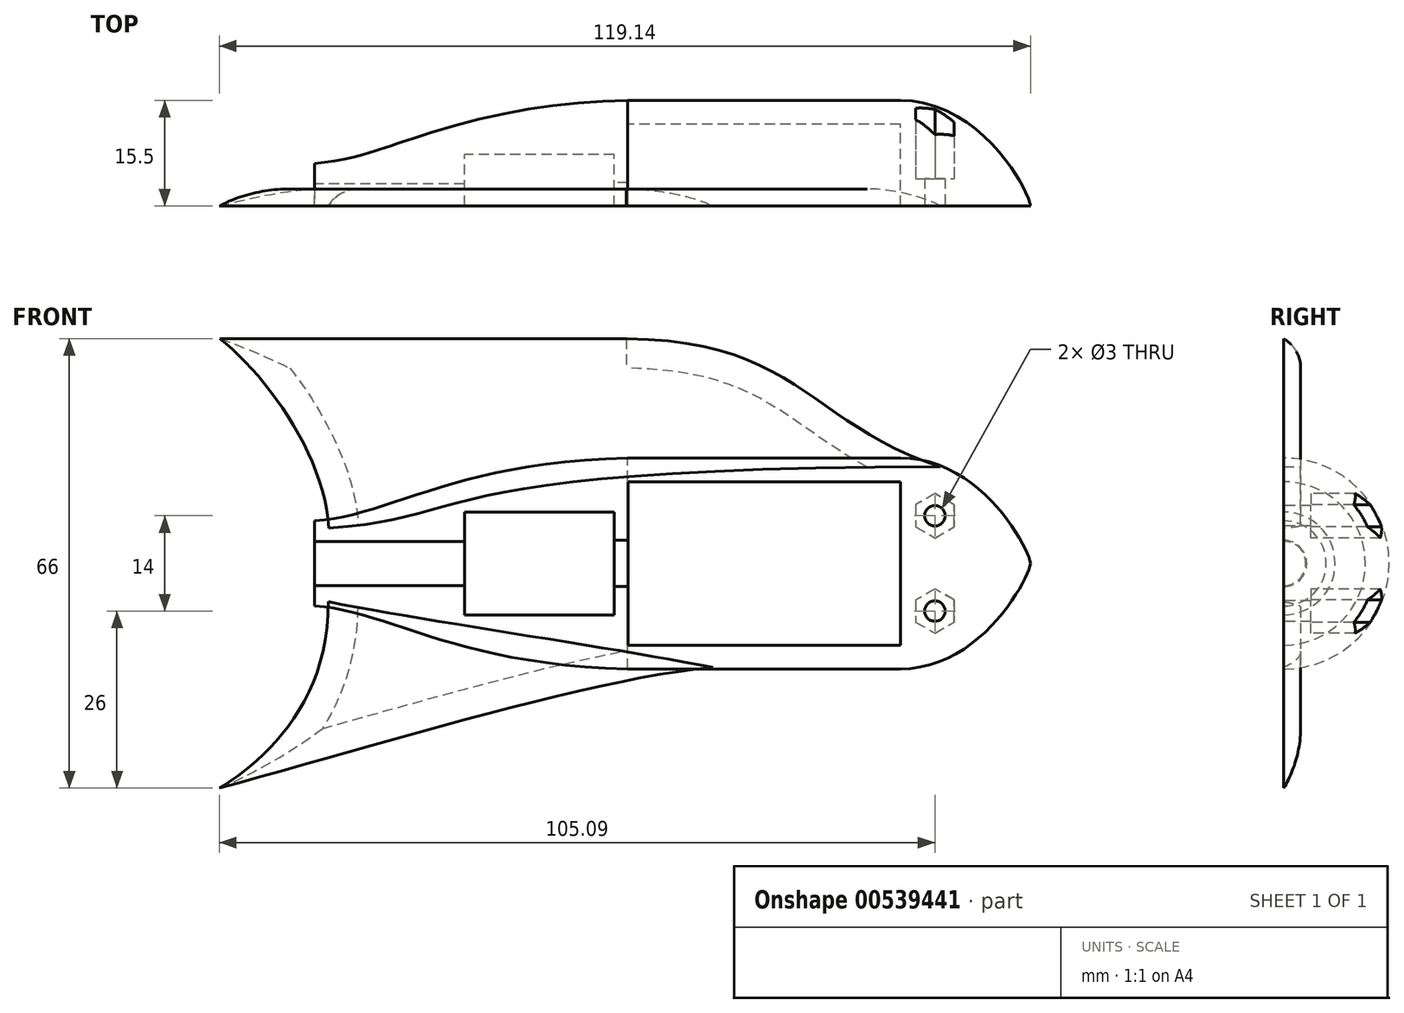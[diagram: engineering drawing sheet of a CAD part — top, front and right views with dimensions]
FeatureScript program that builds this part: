
annotation { "Feature Type Name" : "Feature", "Feature Type Description" : "" }
export const myFeature = defineFeature(function(context is Context, id is Id, definition is map)
    precondition{}
    {
        {
            var Q0;
            Q0=qCreatedBy(makeId("Front.planeOp"),FACE);
            var sketch = newSketch(context, id + "F0", { "sketchPlane" : qUnion([Q0])});
            skLineSegment(sketch, "E0", {"start": v(-75.09, 3.25) * mm, "end": v(-53.09, 3.25) * mm});
            skLineSegment(sketch, "E1", {"start": v(-53.09, 3.25) * mm, "end": v(-53.09, 7.55) * mm});
            skLineSegment(sketch, "E2", {"start": v(-53.09, 7.55) * mm, "end": v(-31.09, 7.55) * mm});
            skLineSegment(sketch, "E3", {"start": v(-31.09, 7.55) * mm, "end": v(-31.09, 3.4) * mm});
            skLineSegment(sketch, "E4", {"start": v(-31.09, 3.4) * mm, "end": v(-29.09, 3.4) * mm});
            skLineSegment(sketch, "E5", {"start": v(-29.09, 3.4) * mm, "end": v(-29.09, 12) * mm});
            skLineSegment(sketch, "E6", {"start": v(-29.09, 12) * mm, "end": v(10.91, 12) * mm});
            skLineSegment(sketch, "E7", {"start": v(10.91, 12) * mm, "end": v(10.91, 0) * mm});
            skLineSegment(sketch, "E8", {"start": v(10.91, 0) * mm, "end": v(30.05, 0) * mm});
            skLineSegment(sketch, "E9", {"start": v(-75.09, 6.25) * mm, "end": v(-75.09, 3.25) * mm});
            skLineSegment(sketch, "E10", {"start": v(10.91, 15.5) * mm, "end": v(-29.14, 15.5) * mm});
            skFitSpline(sketch, "E11", {"points": [v(30.05, 0) * mm, v(10.91, 15.5) * mm], "startDerivative": vector(-1.53, 7.93) * mm, "endDerivative": vector(-35.34, 0.06) * mm});
            skLineSegment(sketch, "E12", {"start": v(-31.09, 3.4) * mm, "end": v(-31.09, 0) * mm});
            skFitSpline(sketch, "E13", {"points": [v(-29.14, 15.5) * mm, v(-75.09, 6.25) * mm], "startDerivative": vector(-76.48, -1.84) * mm, "endDerivative": vector(-32.8, -2) * mm});
            skLineSegment(sketch, "E14", {"start": v(-53.09, 3.25) * mm, "end": v(-53.09, 0) * mm});
            skSolve(sketch);
        }
        {
            var Q0;
            Q0=makeQuery(id+"F0.imprint","IMPRINT",FACE,{"disambiguationData":[TD([[makeQuery(id+"F0.imprint","IMPRINT",EDGE,{"derivedFrom":sQuery(id+"F0.wireOp",EDGE,"E0")}),1.0]])]});
            var Q1;
            Q1=sQuery(id+"F0.wireOp",EDGE,"E8");
            revolve(context, id + "F1", {"entities" : qUnion([Q0]), "axis" : qUnion([Q1]), "revolveType" : RevolveType.ONE_DIRECTION, "angle" : 180 * degree});
        }
        {
            var Q0;
            Q0=qCreatedBy(makeId("Front.planeOp"),FACE);
            var sketch = newSketch(context, id + "F2", { "sketchPlane" : qUnion([Q0])});
            skFitSpline(sketch, "E15.MirrorCS", {"points": [v(-89.1, -33) * mm, v(-73.1, -5.62) * mm], "startDerivative": vector(19.99, 12.25) * mm, "endDerivative": vector(-0.31, 44.72) * mm});
            skFitSpline(sketch, "E16.MirrorCS", {"points": [v(-73.1, -5.63) * mm, v(-16.62, -15.27) * mm], "startDerivative": vector(45.64, -9.01) * mm, "endDerivative": vector(45.64, -9.01) * mm});
            skFitSpline(sketch, "E17", {"points": [v(-16.62, -15.27) * mm, v(-89.1, -33) * mm], "startDerivative": vector(-54.11, -4.81) * mm, "endDerivative": vector(-66.28, -18) * mm});
            skSolve(sketch);
        }
        {
            var Q0;
            Q0=qCreatedBy(makeId("Front.planeOp"),FACE);
            var sketch = newSketch(context, id + "F3", { "sketchPlane" : qUnion([Q0])});
            skFitSpline(sketch, "E18", {"points": [v(-72.99, 5.2) * mm, v(16.8, 14.22) * mm], "startDerivative": vector(68.22, 4.63) * mm, "endDerivative": vector(232.35, 0.67) * mm});
            skFitSpline(sketch, "E19", {"points": [v(16.8, 14.22) * mm, v(-29.28, 33) * mm], "startDerivative": vector(-57.2, 18.37) * mm, "endDerivative": vector(-76.22, 0.95) * mm});
            skFitSpline(sketch, "E20", {"points": [v(-29.28, 33) * mm, v(-88.99, 33) * mm], "startDerivative": vector(-55.16, 0) * mm, "endDerivative": vector(-55.16, 0) * mm});
            skFitSpline(sketch, "E21", {"points": [v(-88.99, 33) * mm, v(-72.99, 5.2) * mm], "startDerivative": vector(21.07, -16.51) * mm, "endDerivative": vector(1.77, -31.08) * mm});
            skSolve(sketch);
        }
        {
            var Q0;
            Q0=qSketchRegion(id+"F3",true);
            extrude(context, id + "F4", {"entities" : qUnion([Q0]), "depth" : 2.5 * mm, "offsetDistance" : 25 * mm});
        }
        {
            var Q0;
            Q0=makeQuery(id+"F4.opExtrude","CAP_EDGE",EDGE,{"disambiguationData":[OSD([sQuery(id+"F3.wireOp",EDGE,"E20")])],"isStart":false});
            var Q1;
            Q1=makeQuery(id+"F4.opExtrude","CAP_EDGE",EDGE,{"disambiguationData":[OSD([sQuery(id+"F3.wireOp",EDGE,"E19")])],"isStart":false});
            fillet(context, id + "F5", {"entities" : qUnion([Q0, Q1]), "radius" : 5 * mm, "tangentPropagation" : true, "allowEdgeOverflow" : false});
        }
        {
            var Q0;
            Q0=makeQuery(id+"F5.opFillet","BLEND_EDGE",EDGE,{"blendedFrom":[makeQuery(id+"F4.opExtrude","CAP_EDGE",EDGE,{"disambiguationData":[OSD([sQuery(id+"F3.wireOp",EDGE,"E20")])],"isStart":false}),makeQuery(id+"F4.opExtrude","SWEPT_FACE",FACE,{"disambiguationData":[OSD([sQuery(id+"F3.wireOp",EDGE,"E21")])]})],"blendedInto":[makeQuery(id+"F4.opExtrude","SWEPT_FACE",FACE,{"disambiguationData":[OSD([sQuery(id+"F3.wireOp",EDGE,"E21")])]})]});
            fillet(context, id + "F6", {"entities" : qUnion([Q0]), "radius" : 5 * mm, "tangentPropagation" : true, "allowEdgeOverflow" : false});
        }
        {
            var Q0;
            Q0=makeQuery(id+"F2.imprint","IMPRINT",FACE,{"disambiguationData":[TD([[makeQuery(id+"F2.imprint","IMPRINT",EDGE,{"derivedFrom":sQuery(id+"F2.wireOp",EDGE,"E15.MirrorCS")}),-1.0]])]});
            extrude(context, id + "F7", {"entities" : qUnion([Q0]), "depth" : 2.5 * mm, "offsetDistance" : 25 * mm});
        }
        {
            var Q0;
            Q0=makeQuery(id+"F7.opExtrude","CAP_EDGE",EDGE,{"disambiguationData":[OSD([sQuery(id+"F2.wireOp",EDGE,"E15.MirrorCS")])],"isStart":false});
            fillet(context, id + "F8", {"entities" : qUnion([Q0]), "radius" : 5 * mm, "tangentPropagation" : true, "allowEdgeOverflow" : false});
        }
        {
            var Q0;
            Q0=makeQuery(id+"F7.opExtrude","CAP_EDGE",EDGE,{"disambiguationData":[OSD([sQuery(id+"F2.wireOp",EDGE,"E17")])],"isStart":false});
            fillet(context, id + "F9", {"entities" : qUnion([Q0]), "radius" : 5 * mm, "tangentPropagation" : true, "allowEdgeOverflow" : false});
        }
        {
            var Q0;
            Q0=makeQuery(id+"F1.opRevolve","SWEPT_BODY",BODY,{"disambiguationData":[OSD([sQuery(id+"F0.wireOp",EDGE,"E0"),sQuery(id+"F0.wireOp",EDGE,"E1"),sQuery(id+"F0.wireOp",EDGE,"E2"),sQuery(id+"F0.wireOp",EDGE,"E3"),sQuery(id+"F0.wireOp",EDGE,"E4"),sQuery(id+"F0.wireOp",EDGE,"E5"),sQuery(id+"F0.wireOp",EDGE,"E6"),sQuery(id+"F0.wireOp",EDGE,"E7"),sQuery(id+"F0.wireOp",EDGE,"E8"),sQuery(id+"F0.wireOp",EDGE,"E9"),sQuery(id+"F0.wireOp",EDGE,"E10"),sQuery(id+"F0.wireOp",EDGE,"E11"),sQuery(id+"F0.wireOp",EDGE,"E13")])]});
            var Q1;
            Q1=makeQuery(id+"F7.opExtrude","SWEPT_BODY",BODY,{"disambiguationData":[OSD([sQuery(id+"F2.wireOp",EDGE,"E15.MirrorCS"),sQuery(id+"F2.wireOp",EDGE,"E16.MirrorCS"),sQuery(id+"F2.wireOp",EDGE,"E17")])]});
            var Q2;
            Q2=makeQuery(id+"F4.opExtrude","SWEPT_BODY",BODY,{"disambiguationData":[OSD([sQuery(id+"F3.wireOp",EDGE,"E18"),sQuery(id+"F3.wireOp",EDGE,"E19"),sQuery(id+"F3.wireOp",EDGE,"E20"),sQuery(id+"F3.wireOp",EDGE,"E21")])]});
            var Q3;
            Q3=qCreatedBy(makeId("Front.planeOp"),FACE);
            mirror(context, id + "F10", {"entities" : qUnion([Q0, Q1, Q2]), "mirrorPlane" : qUnion([Q3])});
        }
        {
            var Q0;
            Q0=makeQuery(id+"F1.opRevolve","SWEPT_BODY",BODY,{"disambiguationData":[OSD([sQuery(id+"F0.wireOp",EDGE,"E0"),sQuery(id+"F0.wireOp",EDGE,"E1"),sQuery(id+"F0.wireOp",EDGE,"E2"),sQuery(id+"F0.wireOp",EDGE,"E3"),sQuery(id+"F0.wireOp",EDGE,"E4"),sQuery(id+"F0.wireOp",EDGE,"E5"),sQuery(id+"F0.wireOp",EDGE,"E6"),sQuery(id+"F0.wireOp",EDGE,"E7"),sQuery(id+"F0.wireOp",EDGE,"E8"),sQuery(id+"F0.wireOp",EDGE,"E9"),sQuery(id+"F0.wireOp",EDGE,"E10"),sQuery(id+"F0.wireOp",EDGE,"E11"),sQuery(id+"F0.wireOp",EDGE,"E13")])]});
            var Q1;
            Q1=makeQuery(id+"F4.opExtrude","SWEPT_BODY",BODY,{"disambiguationData":[OSD([sQuery(id+"F3.wireOp",EDGE,"E18"),sQuery(id+"F3.wireOp",EDGE,"E19"),sQuery(id+"F3.wireOp",EDGE,"E20"),sQuery(id+"F3.wireOp",EDGE,"E21")])]});
            var Q2;
            Q2=makeQuery(id+"F7.opExtrude","SWEPT_BODY",BODY,{"disambiguationData":[OSD([sQuery(id+"F2.wireOp",EDGE,"E15.MirrorCS"),sQuery(id+"F2.wireOp",EDGE,"E16.MirrorCS"),sQuery(id+"F2.wireOp",EDGE,"E17")])]});
            deleteBodies(context, id + "F11", {"entities" : qUnion([Q0, Q1, Q2])});
        }
        {
            var Q0;
            Q0=qCreatedBy(makeId("Front.planeOp"),FACE);
            var sketch = newSketch(context, id + "F12", { "sketchPlane" : qUnion([Q0])});
            skCircle(sketch, "E22", {"center": v(0, 0) * mm, "radius": 1.5 * mm});
            skSolve(sketch);
        }
        {
            var Q0;
            Q0 = qSketchRegion(id + "F12", true);
            extrude(context, id + "F13", {"entities" : qUnion([Q0]), "depth" : -4 * mm, "offsetDistance" : 25 * mm});
        }
        {
            var Q0;
            Q0=makeQuery(id+"F13.opExtrude","CAP_FACE",FACE,{"disambiguationData":[OSD([sQuery(id+"F12.wireOp",EDGE,"E22")])],"isStart":false});
            var sketch = newSketch(context, id + "F14", { "sketchPlane" : qUnion([Q0])});
            skCircle(sketch, "E23.cCircle", {"center": v(0, 0) * mm, "radius": 2.82 * mm});
            skLineSegment(sketch, "E23.0", {"start": v(2.82, 1.63) * mm, "end": v(2.82, -1.63) * mm});
            skLineSegment(sketch, "E23.1", {"start": v(2.82, -1.63) * mm, "end": v(0, -3.26) * mm});
            skLineSegment(sketch, "E23.2", {"start": v(0, -3.26) * mm, "end": v(-2.82, -1.63) * mm});
            skLineSegment(sketch, "E23.3", {"start": v(-2.82, -1.63) * mm, "end": v(-2.82, 1.63) * mm});
            skLineSegment(sketch, "E23.4", {"start": v(-2.82, 1.63) * mm, "end": v(0, 3.26) * mm});
            skLineSegment(sketch, "E23.5", {"start": v(0, 3.26) * mm, "end": v(2.82, 1.63) * mm});
            skPoint(sketch, "E23.0.midPoint", {"position": v(2.82, 0) * mm});
            skSolve(sketch);
        }
        {
            var Q0;
            Q0=makeQuery(id+"F14.imprint","IMPRINT",FACE,{"disambiguationData":[TD([[makeQuery(id+"F14.imprint","IMPRINT",EDGE,{"derivedFrom":makeQuery(id+"F13.opExtrude","CAP_EDGE",EDGE,{"disambiguationData":[OSD([sQuery(id+"F12.wireOp",EDGE,"E22")])],"isStart":false})}),1.0]])]});
            var Q1;
            {var subQ0=sQuery(id+"F14.wireOp",EDGE,"E23.4");var subQ1=sQuery(id+"F14.wireOp",EDGE,"E23.cCircle");var subQ2=makeQuery(id+"F14.imprint","INTERSECT",VERTEX,{"derivedFrom":[subQ1,subQ0]});Q1=makeQuery(id+"F14.imprint","IMPRINT",FACE,{"disambiguationData":[TD([[makeQuery(id+"F14.imprint","IMPRINT",EDGE,{"disambiguationData":[TD([[subQ2,-1.0]])],"derivedFrom":subQ1}),-1.0]])]});}
            var Q2;
            {var subQ0=sQuery(id+"F14.wireOp",EDGE,"E23.5");var subQ1=sQuery(id+"F14.wireOp",EDGE,"E23.cCircle");var subQ2=makeQuery(id+"F14.imprint","INTERSECT",VERTEX,{"derivedFrom":[subQ1,subQ0]});Q2=makeQuery(id+"F14.imprint","IMPRINT",FACE,{"disambiguationData":[TD([[makeQuery(id+"F14.imprint","IMPRINT",EDGE,{"disambiguationData":[TD([[subQ2,-1.0]])],"derivedFrom":subQ1}),-1.0]])]});}
            var Q3;
            {var subQ0=sQuery(id+"F14.wireOp",EDGE,"E23.5");var subQ1=sQuery(id+"F14.wireOp",EDGE,"E23.cCircle");var subQ2=makeQuery(id+"F14.imprint","INTERSECT",VERTEX,{"derivedFrom":[subQ1,subQ0]});Q3=makeQuery(id+"F14.imprint","IMPRINT",FACE,{"disambiguationData":[TD([[makeQuery(id+"F14.imprint","IMPRINT",EDGE,{"disambiguationData":[TD([[subQ2,1.0]])],"derivedFrom":subQ1}),-1.0]])]});}
            var Q4;
            {var subQ0=sQuery(id+"F14.wireOp",EDGE,"E23.0");var subQ1=sQuery(id+"F14.wireOp",EDGE,"E23.cCircle");var subQ2=makeQuery(id+"F14.imprint","INTERSECT",VERTEX,{"derivedFrom":[subQ1,subQ0]});Q4=makeQuery(id+"F14.imprint","IMPRINT",FACE,{"disambiguationData":[TD([[makeQuery(id+"F14.imprint","IMPRINT",EDGE,{"disambiguationData":[TD([[subQ2,1.0]])],"derivedFrom":subQ1}),-1.0]])]});}
            var Q5;
            {var subQ0=sQuery(id+"F14.wireOp",EDGE,"E23.2");var subQ1=sQuery(id+"F14.wireOp",EDGE,"E23.cCircle");var subQ2=makeQuery(id+"F14.imprint","INTERSECT",VERTEX,{"derivedFrom":[subQ1,subQ0]});Q5=makeQuery(id+"F14.imprint","IMPRINT",FACE,{"disambiguationData":[TD([[makeQuery(id+"F14.imprint","IMPRINT",EDGE,{"disambiguationData":[TD([[subQ2,-1.0]])],"derivedFrom":subQ1}),-1.0]])]});}
            var Q6;
            {var subQ0=sQuery(id+"F14.wireOp",EDGE,"E23.3");var subQ1=sQuery(id+"F14.wireOp",EDGE,"E23.cCircle");var subQ2=makeQuery(id+"F14.imprint","INTERSECT",VERTEX,{"derivedFrom":[subQ1,subQ0]});Q6=makeQuery(id+"F14.imprint","IMPRINT",FACE,{"disambiguationData":[TD([[makeQuery(id+"F14.imprint","IMPRINT",EDGE,{"disambiguationData":[TD([[subQ2,-1.0]])],"derivedFrom":subQ1}),-1.0]])]});}
            var Q7;
            Q7=makeQuery(id+"F14.imprint","IMPRINT",FACE,{"disambiguationData":[TD([[makeQuery(id+"F14.imprint","IMPRINT",EDGE,{"derivedFrom":makeQuery(id+"F13.opExtrude","CAP_EDGE",EDGE,{"disambiguationData":[OSD([sQuery(id+"F12.wireOp",EDGE,"E22")])],"isStart":false})}),-1.0]])]});
            extrude(context, id + "F15", {"entities" : qUnion([Q0, Q1, Q2, Q3, Q4, Q5, Q6, Q7]), "depth" : 15 * mm, "offsetDistance" : 25 * mm});
        }
        {
            var Q0;
            Q0=makeQuery(id+"F15.opExtrude","SWEPT_BODY",BODY,{"disambiguationData":[OSD([sQuery(id+"F14.wireOp",EDGE,"E23.0"),sQuery(id+"F14.wireOp",EDGE,"E23.1"),sQuery(id+"F14.wireOp",EDGE,"E23.2"),sQuery(id+"F14.wireOp",EDGE,"E23.3"),sQuery(id+"F14.wireOp",EDGE,"E23.4"),sQuery(id+"F14.wireOp",EDGE,"E23.5")])]});
            var Q1;
            Q1=makeQuery(id+"F13.opExtrude","SWEPT_BODY",BODY,{"disambiguationData":[OSD([sQuery(id+"F12.wireOp",EDGE,"E22")])]});
            transform(context, id + "F16", {"entities" : qUnion([Q0, Q1]), "transformType" : TransformType.TRANSLATION_3D, "dx" : 16 * mm, "dy" : 0 * mm, "dz" : 7 * mm, "makeCopy" : false});
        }
        {
            var Q0;
            Q0=makeQuery(id+"F15.opExtrude","SWEPT_BODY",BODY,{"disambiguationData":[OSD([sQuery(id+"F14.wireOp",EDGE,"E23.0"),sQuery(id+"F14.wireOp",EDGE,"E23.1"),sQuery(id+"F14.wireOp",EDGE,"E23.2"),sQuery(id+"F14.wireOp",EDGE,"E23.3"),sQuery(id+"F14.wireOp",EDGE,"E23.4"),sQuery(id+"F14.wireOp",EDGE,"E23.5")])]});
            var Q1;
            Q1=makeQuery(id+"F13.opExtrude","SWEPT_BODY",BODY,{"disambiguationData":[OSD([sQuery(id+"F12.wireOp",EDGE,"E22")])]});
            transform(context, id + "F17", {"entities" : qUnion([Q0, Q1]), "transformType" : TransformType.TRANSLATION_3D, "dx" : 0 * mm, "dy" : 0 * mm, "dz" : -14 * mm, "makeCopy" : true});
        }
        {
            var Q0;
            Q0=makeQuery(id+"F17.opPattern","COPY",BODY,{"derivedFrom":makeQuery(id+"F15.opExtrude","SWEPT_BODY",BODY,{"disambiguationData":[OSD([sQuery(id+"F14.wireOp",EDGE,"E23.0"),sQuery(id+"F14.wireOp",EDGE,"E23.1"),sQuery(id+"F14.wireOp",EDGE,"E23.2"),sQuery(id+"F14.wireOp",EDGE,"E23.3"),sQuery(id+"F14.wireOp",EDGE,"E23.4"),sQuery(id+"F14.wireOp",EDGE,"E23.5")])]}),"instanceName":"1"});
            var Q1;
            Q1=makeQuery(id+"F10.opPattern","COPY",BODY,{"derivedFrom":makeQuery(id+"F1.opRevolve","SWEPT_BODY",BODY,{"disambiguationData":[OSD([sQuery(id+"F0.wireOp",EDGE,"E0"),sQuery(id+"F0.wireOp",EDGE,"E1"),sQuery(id+"F0.wireOp",EDGE,"E2"),sQuery(id+"F0.wireOp",EDGE,"E3"),sQuery(id+"F0.wireOp",EDGE,"E4"),sQuery(id+"F0.wireOp",EDGE,"E5"),sQuery(id+"F0.wireOp",EDGE,"E6"),sQuery(id+"F0.wireOp",EDGE,"E7"),sQuery(id+"F0.wireOp",EDGE,"E8"),sQuery(id+"F0.wireOp",EDGE,"E9"),sQuery(id+"F0.wireOp",EDGE,"E10"),sQuery(id+"F0.wireOp",EDGE,"E11"),sQuery(id+"F0.wireOp",EDGE,"E13")])]}),"instanceName":"1"});
            booleanBodies(context, id + "F18", {"operationType" : BooleanOperationType.SUBTRACTION, "tools" : qUnion([Q0]), "targets" : qUnion([Q1])});
        }
        {
            var Q0;
            Q0=makeQuery(id+"F15.opExtrude","SWEPT_BODY",BODY,{"disambiguationData":[OSD([sQuery(id+"F14.wireOp",EDGE,"E23.0"),sQuery(id+"F14.wireOp",EDGE,"E23.1"),sQuery(id+"F14.wireOp",EDGE,"E23.2"),sQuery(id+"F14.wireOp",EDGE,"E23.3"),sQuery(id+"F14.wireOp",EDGE,"E23.4"),sQuery(id+"F14.wireOp",EDGE,"E23.5")])]});
            var Q1;
            Q1=makeQuery(id+"F10.opPattern","COPY",BODY,{"derivedFrom":makeQuery(id+"F1.opRevolve","SWEPT_BODY",BODY,{"disambiguationData":[OSD([sQuery(id+"F0.wireOp",EDGE,"E0"),sQuery(id+"F0.wireOp",EDGE,"E1"),sQuery(id+"F0.wireOp",EDGE,"E2"),sQuery(id+"F0.wireOp",EDGE,"E3"),sQuery(id+"F0.wireOp",EDGE,"E4"),sQuery(id+"F0.wireOp",EDGE,"E5"),sQuery(id+"F0.wireOp",EDGE,"E6"),sQuery(id+"F0.wireOp",EDGE,"E7"),sQuery(id+"F0.wireOp",EDGE,"E8"),sQuery(id+"F0.wireOp",EDGE,"E9"),sQuery(id+"F0.wireOp",EDGE,"E10"),sQuery(id+"F0.wireOp",EDGE,"E11"),sQuery(id+"F0.wireOp",EDGE,"E13")])]}),"instanceName":"1"});
            booleanBodies(context, id + "F19", {"operationType" : BooleanOperationType.SUBTRACTION, "tools" : qUnion([Q0]), "targets" : qUnion([Q1])});
        }
        {
            var Q0;
            Q0=makeQuery(id+"F13.opExtrude","SWEPT_BODY",BODY,{"disambiguationData":[OSD([sQuery(id+"F12.wireOp",EDGE,"E22")])]});
            var Q1;
            Q1=makeQuery(id+"F10.opPattern","COPY",BODY,{"derivedFrom":makeQuery(id+"F1.opRevolve","SWEPT_BODY",BODY,{"disambiguationData":[OSD([sQuery(id+"F0.wireOp",EDGE,"E0"),sQuery(id+"F0.wireOp",EDGE,"E1"),sQuery(id+"F0.wireOp",EDGE,"E2"),sQuery(id+"F0.wireOp",EDGE,"E3"),sQuery(id+"F0.wireOp",EDGE,"E4"),sQuery(id+"F0.wireOp",EDGE,"E5"),sQuery(id+"F0.wireOp",EDGE,"E6"),sQuery(id+"F0.wireOp",EDGE,"E7"),sQuery(id+"F0.wireOp",EDGE,"E8"),sQuery(id+"F0.wireOp",EDGE,"E9"),sQuery(id+"F0.wireOp",EDGE,"E10"),sQuery(id+"F0.wireOp",EDGE,"E11"),sQuery(id+"F0.wireOp",EDGE,"E13")])]}),"instanceName":"1"});
            booleanBodies(context, id + "F20", {"operationType" : BooleanOperationType.SUBTRACTION, "tools" : qUnion([Q0]), "targets" : qUnion([Q1])});
        }
        {
            var Q0;
            Q0=makeQuery(id+"F17.opPattern","COPY",BODY,{"derivedFrom":makeQuery(id+"F13.opExtrude","SWEPT_BODY",BODY,{"disambiguationData":[OSD([sQuery(id+"F12.wireOp",EDGE,"E22")])]}),"instanceName":"1"});
            var Q1;
            Q1=makeQuery(id+"F10.opPattern","COPY",BODY,{"derivedFrom":makeQuery(id+"F1.opRevolve","SWEPT_BODY",BODY,{"disambiguationData":[OSD([sQuery(id+"F0.wireOp",EDGE,"E0"),sQuery(id+"F0.wireOp",EDGE,"E1"),sQuery(id+"F0.wireOp",EDGE,"E2"),sQuery(id+"F0.wireOp",EDGE,"E3"),sQuery(id+"F0.wireOp",EDGE,"E4"),sQuery(id+"F0.wireOp",EDGE,"E5"),sQuery(id+"F0.wireOp",EDGE,"E6"),sQuery(id+"F0.wireOp",EDGE,"E7"),sQuery(id+"F0.wireOp",EDGE,"E8"),sQuery(id+"F0.wireOp",EDGE,"E9"),sQuery(id+"F0.wireOp",EDGE,"E10"),sQuery(id+"F0.wireOp",EDGE,"E11"),sQuery(id+"F0.wireOp",EDGE,"E13")])]}),"instanceName":"1"});
            booleanBodies(context, id + "F21", {"operationType" : BooleanOperationType.SUBTRACTION, "tools" : qUnion([Q0]), "targets" : qUnion([Q1])});
        }
    });
